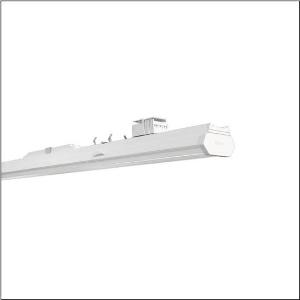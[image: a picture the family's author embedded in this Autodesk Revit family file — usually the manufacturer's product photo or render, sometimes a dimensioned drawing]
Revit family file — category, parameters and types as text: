
# Revit family: licross_11_protected_ho_51tp11mn4gxs
name_source: partatom
category: Lighting Fixtures
units: mm (PartAtom-declared; Revit-internal decimal feet)

## family parameters
Cut with Voids When Loaded = No
Host = Face
Light Source = No
Part Type = Normal
Room Calculation Point = No
Round Connector Dimension = Use Diameter
Shared = No

## types (1)
- --- (1 x LED, 16070 lm, 87.4 W, 4000K)
    Apparent Load = 87 VA
    CIE Flux Codes = 84 94 98 99 100
    Color Rendering = 80
    Color Temperature = 4000K
    Default Elevation = 1800 mm
    Description = Licross 11 Protected HO, luminaire insert, of sheet steel, galvanised, coil coated, white, length: 1.500mm, width: 90mm, height: 101mm, LED rated luminous flux: 16.070lm, light colour: 840, SDCM (Standard Deviation of Colour Matching)MacAdam ≤ 2 SDCM (initial), control gear: ON/OFF Multilumen, with plug, 3-pole, with phase selection, mains connection: 220..240V, AC, 50/60Hz, rated input power: 87W, internal wiring halogen-free, primary light control with lens, of plastic, primary optical cover: cover, of PMMA, light emission: direct distribution, primary light characteristic: symmetric, protection rating (complete): IP64, insulation class (complete): insulation class I (protective earthing), certification: CE, ENEC, VDE, UKCA, protection symbol: D if used in an environment with conductive dust loads with corresponding accessories, impact resistance: IK06, permissible ambient temperature for indoor applications: -35..+35°C, corresponds to IFS (International Featured Standards) requirements for safety and quality in the food industry, reducing of maximum allowable ambient temperature of 5°C with ceiling mounting, LABS conformity tested according to VDMA 24364:2018-05, The light source and the operating device comply with the requirements of the Ecodesign Regulation (EU) 2019/2020 and are replaceable in accordance with this regulation, packaging unit: 1 piece
    Height = 92 mm
    Lamp = 1 x LED
    Lamp Light Flux = 16070 lm
    Lamp Power = 87.4 W
    Lamp count = 1
    Length = 1500 mm
    Luminous efficacy = 184 lm/W
    Manufacturer = Siteco
    ModVariant = No
    Model = 51TP11MN4GXS
    Mounting Place = Ceiling
    Mounting Type = Pendant
    Number of Poles = 1
    OnlyDefault = Yes
    Power Factor = 1
    Product Name = Licross 11 Protected HO
    Product group = luminaire insert | ceiling pendant
    ProductGroupID = 901
    Protection Class = Protection class I
    Protection Degree = IP 64
    RLX_Detail_Level = 1
    RLX_Emergency_Light_Flux = 0 lm
    RLX_Emergency_Type = 0
    RLX_Emergency_Type_DB = No
    RlxData = <blob elided: 22245 chars, md5=cd4634f3>
    Socket = socket
    Standby Power = 0 W
    System Light Flux = 16070 lm
    System Power = 87 W
    Type Comments = factory setting: luminous flux: 100 % | (A | C | E) | 203 mA
    Type Image = l_1256148.jpg
    URL = http://relux.com
    VarID = @adj_091977
    Voltage = 0 V
    Weight = 0.00 kg
    Width = 88 mm

## geometry (parser evidence)
native form markers: Blend x4, Sweep x13
no freeform markers — native parametric forms only
